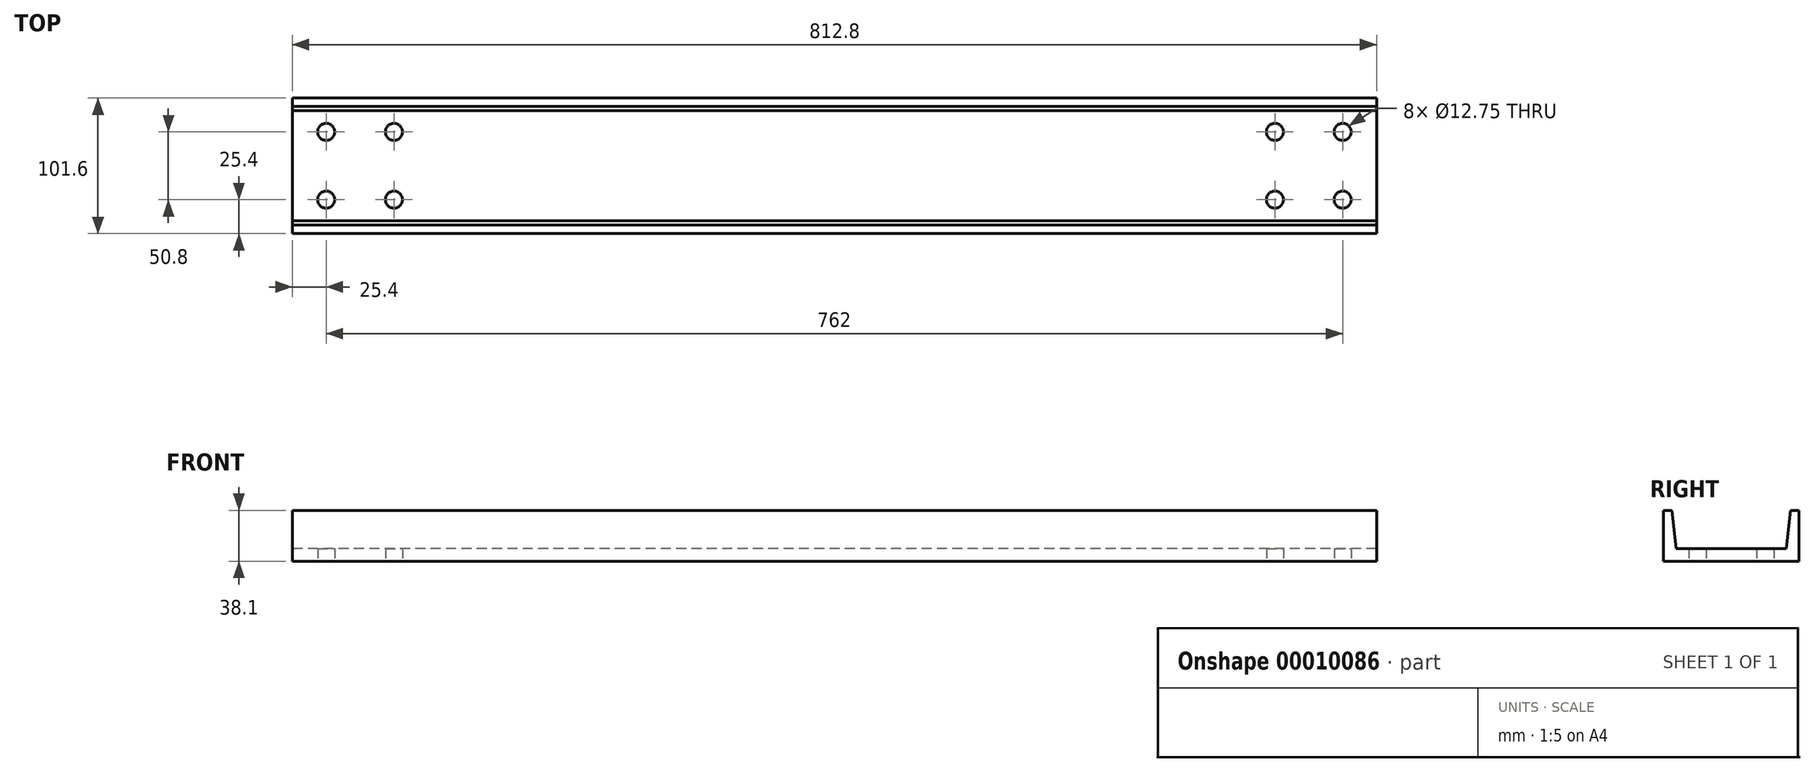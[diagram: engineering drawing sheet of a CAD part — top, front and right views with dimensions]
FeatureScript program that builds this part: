
annotation { "Feature Type Name" : "Feature", "Feature Type Description" : "" }
export const myFeature = defineFeature(function(context is Context, id is Id, definition is map)
    precondition{}
    {
        {
            var Q0;
            Q0=qCreatedBy(makeId("Right.planeOp"),FACE);
            var sketch = newSketch(context, id + "F0", { "sketchPlane" : qUnion([Q0])});
            skLineSegment(sketch, "E0", {"start": v(-44.45, 38.1) * mm, "end": v(-50.8, 38.1) * mm});
            skLineSegment(sketch, "E1", {"start": v(-50.8, 38.1) * mm, "end": v(-50.8, 0) * mm});
            skLineSegment(sketch, "E2", {"start": v(-50.8, 0) * mm, "end": v(0, 0) * mm});
            skLineSegment(sketch, "E3", {"start": v(0, 0) * mm, "end": v(50.8, 0) * mm});
            skLineSegment(sketch, "E4", {"start": v(50.8, 0) * mm, "end": v(50.8, 38.1) * mm});
            skLineSegment(sketch, "E5", {"start": v(50.8, 38.1) * mm, "end": v(44.45, 38.1) * mm});
            skLineSegment(sketch, "E6", {"start": v(44.45, 38.1) * mm, "end": v(41.27, 9.52) * mm});
            skLineSegment(sketch, "E7", {"start": v(41.28, 9.53) * mm, "end": v(0, 9.53) * mm});
            skLineSegment(sketch, "E8", {"start": v(0, 9.52) * mm, "end": v(-41.28, 9.52) * mm});
            skLineSegment(sketch, "E9", {"start": v(-41.27, 9.52) * mm, "end": v(-44.45, 38.1) * mm});
            skSolve(sketch);
        }
        {
            var Q0;
            Q0 = qSketchRegion(id + "F0", true);
            extrude(context, id + "F1", {"entities" : qUnion([Q0]), "endBound" : BoundingType.SYMMETRIC, "depth" : 812.8 * mm});
        }
        {
            var Q0;
            Q0=makeQuery(id+"F1.opExtrude","SWEPT_FACE",FACE,{"disambiguationData":[OSD([sQuery(id+"F0.wireOp",EDGE,"E2"),sQuery(id+"F0.wireOp",EDGE,"E3")])]});
            var sketch = newSketch(context, id + "F2", { "sketchPlane" : qUnion([Q0])});
            skCircle(sketch, "E10", {"center": v(330.2, 25.4) * mm, "radius": 6.38 * mm});
            skCircle(sketch, "E11", {"center": v(330.2, -25.4) * mm, "radius": 6.38 * mm});
            skCircle(sketch, "E12", {"center": v(381, 25.4) * mm, "radius": 6.38 * mm});
            skCircle(sketch, "E13", {"center": v(381, -25.4) * mm, "radius": 6.38 * mm});
            skCircle(sketch, "E14", {"center": v(-330.2, 25.4) * mm, "radius": 6.38 * mm});
            skCircle(sketch, "E15", {"center": v(-330.2, -25.4) * mm, "radius": 6.38 * mm});
            skCircle(sketch, "E16", {"center": v(-381, 25.4) * mm, "radius": 6.38 * mm});
            skCircle(sketch, "E17", {"center": v(-381, -25.4) * mm, "radius": 6.38 * mm});
            skLineSegment(sketch, "E18", {"start": v(381, 25.4) * mm, "end": v(381, -25.4) * mm});
            skLineSegment(sketch, "E19", {"start": v(381, 0) * mm, "end": v(406.4, 0) * mm});
            skLineSegment(sketch, "E20", {"start": v(-381, 25.4) * mm, "end": v(-381, -25.4) * mm});
            skLineSegment(sketch, "E21", {"start": v(-381, 0) * mm, "end": v(-406.4, 0) * mm});
            skSolve(sketch);
        }
        {
            var Q0;
            Q0 = qSketchRegion(id + "F2", true);
            extrude(context, id + "F3", {"entities" : qUnion([Q0]), "operationType" : NewBodyOperationType.REMOVE, "endBound" : BoundingType.THROUGH_ALL, "oppositeDirection" : true, "depth" : 25.4 * mm});
        }
    });
